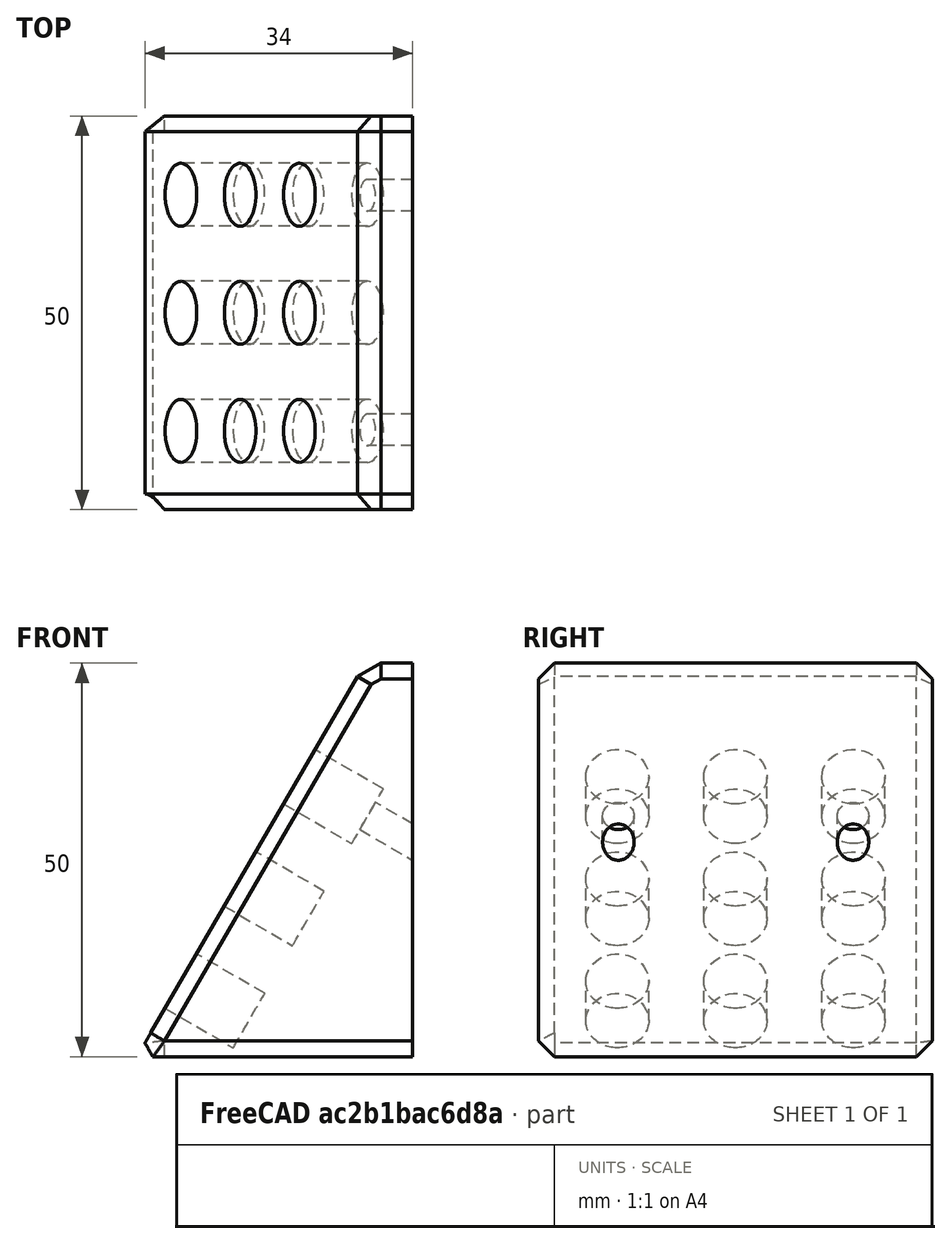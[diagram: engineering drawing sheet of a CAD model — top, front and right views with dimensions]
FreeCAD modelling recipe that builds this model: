
FCSTD DOCUMENT  (FreeCAD 0.19R)
Label: bitholder
License: All rights reserved
LicenseURL: http://en.wikipedia.org/wiki/All_rights_reserved
objects: Sketcher::SketchObject×3, PartDesign::Pocket×2, PartDesign::Pad×1, PartDesign::Chamfer×1, PartDesign::Body×1, Mesh::Feature×1
note: 12 computed .brp shape members not serialized (recipe doc carries the construction recipe); baked Part::Feature solids carry a one-line shape summary decoded from their .brp

FEATURE [Sketcher::SketchObject] Sketch
  FullyConstrained = true
  MapMode = 5
  Placement = pos=(0,0,0) rot=(1,0,0;1.5708rad)
  Support = -> [XZ_Plane]
  sketch-geometry (4):
    g0: LineSegment StartX=0 StartY=50 StartZ=0 EndX=0 EndY=0 EndZ=0
    g1: LineSegment StartX=0 StartY=0 StartZ=0 EndX=-35 EndY=0 EndZ=0
    g2: LineSegment StartX=-35 StartY=0 StartZ=0 EndX=-6 EndY=50 EndZ=0
    g3: LineSegment StartX=-6 StartY=50 StartZ=0 EndX=0 EndY=50 EndZ=0
  constraints (11):
    c: PointOnObject(g0,g-2)
    c: Coincident(g0,g-1)
    c: Coincident(g0,g1)
    c: Horizontal(g1)
    c: Coincident(g2,g3)
    c: Coincident(g3,g0)
    c: Horizontal(g3)
    c: Distance(g3) = 6
    c: Distance(g1) = 35
    c: Distance(g0) = 50
    c: Coincident(g2,g1)
FEATURE [PartDesign::Pad] Pad
  Direction = (1,1,1)
  Length = 50
  Length2 = 100
  Midplane = true
  Placement = pos=(0,0,0) rot=(1,0,0;1.5708rad)
  Profile = -> Sketch
  Type = 0
FEATURE [Sketcher::SketchObject] Sketch002
  FullyConstrained = false
  MapMode = 5
  Placement = pos=(-26.1898,1.01e-14,15.1901) rot=(-0.49914,0,0.866521;3.14159rad)
  Support = -> [Pad]
  sketch-geometry (21):
    g0: Circle CenterX=-23.5405 CenterY=0 CenterZ=0 NormalX=0 NormalY=0 NormalZ=1 AngleXU=0 Radius=4
    g1: Circle CenterX=-8.54046 CenterY=0 CenterZ=0 NormalX=0 NormalY=0 NormalZ=1 AngleXU=0 Radius=4
    g2: Circle CenterX=6.45954 CenterY=0 CenterZ=0 NormalX=0 NormalY=0 NormalZ=1 AngleXU=0 Radius=4
    g3: LineSegment StartX=-23.5405 StartY=0 StartZ=0 EndX=-8.54046 EndY=0 EndZ=0
    g4: LineSegment StartX=-8.54046 StartY=0 StartZ=0 EndX=6.45954 EndY=0 EndZ=0
    g5: LineSegment StartX=-23.5405 StartY=0 StartZ=0 EndX=-23.5405 EndY=15 EndZ=0
    g6: LineSegment StartX=-23.5405 StartY=15 StartZ=0 EndX=-8.54046 EndY=15 EndZ=0
    g7: LineSegment StartX=-8.54046 StartY=15 StartZ=0 EndX=-8.54046 EndY=0 EndZ=0
    g8: LineSegment StartX=-8.54046 StartY=15 StartZ=0 EndX=6.45954 EndY=15 EndZ=0
    g9: LineSegment StartX=6.45954 StartY=15 StartZ=0 EndX=6.45954 EndY=0 EndZ=0
    g10: LineSegment StartX=6.45954 StartY=0 StartZ=0 EndX=6.45954 EndY=-15 EndZ=0
    g11: LineSegment StartX=6.45954 StartY=-15 StartZ=0 EndX=-8.54046 EndY=-15 EndZ=0
    g12: LineSegment StartX=-8.54046 StartY=-15 StartZ=0 EndX=-8.54046 EndY=0 EndZ=0
    g13: LineSegment StartX=-23.5405 StartY=0 StartZ=0 EndX=-23.5405 EndY=-15 EndZ=0
    g14: LineSegment StartX=-23.5405 StartY=-15 StartZ=0 EndX=-8.54046 EndY=-15 EndZ=0
    g15: Circle CenterX=-23.5405 CenterY=15 CenterZ=0 NormalX=0 NormalY=0 NormalZ=1 AngleXU=0 Radius=4
    g16: Circle CenterX=-8.54046 CenterY=15 CenterZ=0 NormalX=0 NormalY=0 NormalZ=1 AngleXU=0 Radius=4
    g17: Circle CenterX=6.45954 CenterY=15 CenterZ=0 NormalX=0 NormalY=0 NormalZ=1 AngleXU=0 Radius=4
    g18: Circle CenterX=6.45954 CenterY=-15 CenterZ=0 NormalX=0 NormalY=0 NormalZ=1 AngleXU=0 Radius=4
    g19: Circle CenterX=-8.54046 CenterY=-15 CenterZ=0 NormalX=0 NormalY=0 NormalZ=1 AngleXU=0 Radius=4
    g20: Circle CenterX=-23.5405 CenterY=-15 CenterZ=0 NormalX=0 NormalY=0 NormalZ=1 AngleXU=0 Radius=4
  constraints (50):
    c: PointOnObject(g0,g-1)
    c: PointOnObject(g1,g-1)
    c: PointOnObject(g2,g-1)
    c: Diameter(g0) = 8
    c: Equal(g0,g1)
    c: Equal(g0,g2)
    c: Coincident(g3,g0)
    c: Coincident(g4,g2)
    c: Distance(g3) = 15
    c: Coincident(g3,g1)
    c: Coincident(g4,g1)
    c: Equal(g4,g3)
    c: Coincident(g5,g0)
    c: Coincident(g5,g6)
    c: Horizontal(g6)
    c: Coincident(g6,g7)
    c: Coincident(g7,g1)
    c: Vertical(g7)
    c: Coincident(g6,g8)
    c: Horizontal(g8)
    c: Coincident(g8,g9)
    c: Coincident(g9,g2)
    c: Coincident(g10,g2)
    c: Coincident(g10,g11)
    c: Horizontal(g11)
    c: Coincident(g11,g12)
    c: Coincident(g12,g1)
    c: Coincident(g13,g0)
    c: Vertical(g13)
    c: Coincident(g13,g14)
    c: Coincident(g14,g11)
    c: Equal(g9,g10)
    c: Equal(g10,g12)
    c: Equal(g12,g7)
    c: Equal(g7,g5)
    c: Equal(g5,g13)
    c: Vertical(g12)
    c: Distance(g9) = 15
    c: Coincident(g15,g5)
    c: Coincident(g16,g6)
    c: Coincident(g17,g8)
    c: Coincident(g18,g10)
    c: Coincident(g19,g11)
    c: Coincident(g20,g13)
    c: Diameter(g20) = 8
    c: Equal(g20,g19)
    c: Equal(g20,g18)
    c: Equal(g20,g17)
    c: Equal(g20,g16)
    c: Equal(g20,g15)
FEATURE [PartDesign::Pocket] Pocket
  BaseFeature = -> Pad
  Length = 10
  Length2 = 100
  Placement = pos=(0,0,0) rot=(1,0,0;1.5708rad)
  Profile = -> Sketch002
  Type = 0
FEATURE [Sketcher::SketchObject] Sketch003
  FullyConstrained = false
  MapMode = 5
  Placement = pos=(-17.5395,1.32e-14,10.1729) rot=(-0.49914,0,0.866521;3.14159rad)
  Support = -> [Pocket]
  sketch-geometry (2):
    g0: Circle CenterX=-23.583 CenterY=14.8665 CenterZ=0 NormalX=0 NormalY=0 NormalZ=1 AngleXU=0 Radius=2
    g1: Circle CenterX=-23.583 CenterY=-14.9445 CenterZ=0 NormalX=0 NormalY=0 NormalZ=1 AngleXU=0 Radius=2
  constraints (2):
    c: Diameter(g1) = 4
    c: Equal(g1,g0)
FEATURE [PartDesign::Pocket] Pocket001
  BaseFeature = -> Pocket
  Length = 5
  Length2 = 100
  Placement = pos=(0,0,0) rot=(1,0,0;1.5708rad)
  Profile = -> Sketch003
  Type = 1
FEATURE [PartDesign::Chamfer] Chamfer
  Angle = 45
  Base = -> Pocket001 [Edge14,Edge11,Edge10,Edge12,Edge13,Edge7,Edge9,Edge8]
  BaseFeature = -> Pocket001
  ChamferType = 0
  FlipDirection = false
  Placement = pos=(0,0,0) rot=(1,0,0;1.5708rad)
  Size = 2
  Size2 = 1
  SupportTransform = false
FEATURE [PartDesign::Body] Body
  Group = -> [Sketch,Pad,Sketch002,Sketch003,Pocket,Pocket001,Chamfer]
  Origin = -> Origin
  Tip = -> Chamfer
FEATURE [Mesh::Feature] Mesh  label="Chamfer (Meshed)"
